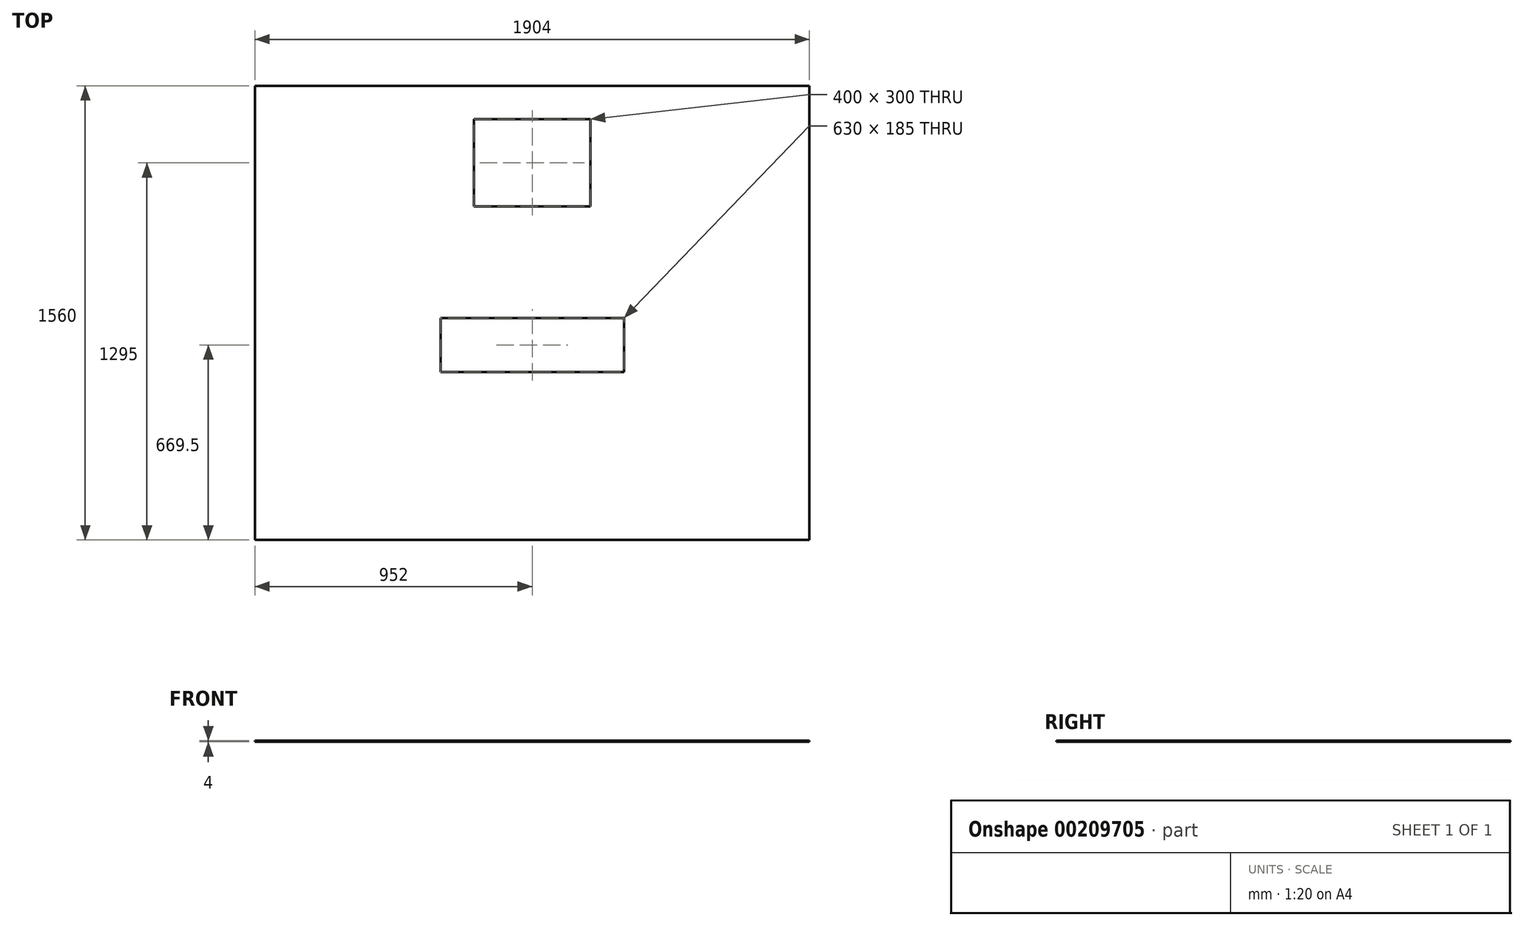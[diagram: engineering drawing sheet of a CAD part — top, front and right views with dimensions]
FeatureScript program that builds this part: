
annotation { "Feature Type Name" : "Feature", "Feature Type Description" : "" }
export const myFeature = defineFeature(function(context is Context, id is Id, definition is map)
    precondition{}
    {
        {
            var Q0;
            Q0=qCreatedBy(makeId("Top.planeOp"),FACE);
            var sketch = newSketch(context, id + "F0", { "sketchPlane" : qUnion([Q0])});
            skLineSegment(sketch, "E0.bottom", {"start": v(952, -780) * mm, "end": v(-952, -780) * mm});
            skLineSegment(sketch, "E0.top", {"start": v(952, 780) * mm, "end": v(-952, 780) * mm});
            skLineSegment(sketch, "E0.left", {"start": v(952, -780) * mm, "end": v(952, 780) * mm});
            skLineSegment(sketch, "E0.right", {"start": v(-952, -780) * mm, "end": v(-952, 780) * mm});
            skPoint(sketch, "E0.middle", {"position": v(0, 0) * mm});
            skSolve(sketch);
        }
        {
            var Q0;
            Q0=qSketchRegion(id+"F0",true);
            extrude(context, id + "F1", {"entities" : qUnion([Q0]), "depth" : 4 * mm});
        }
        {
            var Q0;
            Q0=makeQuery(id+"F1.opExtrude","CAP_FACE",FACE,{"disambiguationData":[OSD([sQuery(id+"F0.wireOp",EDGE,"E0.bottom"),sQuery(id+"F0.wireOp",EDGE,"E0.top"),sQuery(id+"F0.wireOp",EDGE,"E0.left"),sQuery(id+"F0.wireOp",EDGE,"E0.right")])],"isStart":false});
            var sketch = newSketch(context, id + "F2", { "sketchPlane" : qUnion([Q0])});
            skLineSegment(sketch, "E1", {"start": v(0, 780) * mm, "end": v(0, -780) * mm, "construction": true});
            skLineSegment(sketch, "E2.bottom", {"start": v(315, -203) * mm, "end": v(-315, -203) * mm});
            skLineSegment(sketch, "E2.top", {"start": v(315, -18) * mm, "end": v(-315, -18) * mm});
            skLineSegment(sketch, "E2.left", {"start": v(315, -203) * mm, "end": v(315, -18) * mm});
            skLineSegment(sketch, "E2.right", {"start": v(-315, -203) * mm, "end": v(-315, -18) * mm});
            skPoint(sketch, "E2.middle", {"position": v(0, -110.5) * mm});
            skLineSegment(sketch, "E3.bottom", {"start": v(200, 365) * mm, "end": v(-200, 365) * mm});
            skLineSegment(sketch, "E3.top", {"start": v(200, 665) * mm, "end": v(-200, 665) * mm});
            skLineSegment(sketch, "E3.left", {"start": v(200, 365) * mm, "end": v(200, 665) * mm});
            skLineSegment(sketch, "E3.right", {"start": v(-200, 365) * mm, "end": v(-200, 665) * mm});
            skPoint(sketch, "E3.middle", {"position": v(0, 515) * mm});
            skSolve(sketch);
        }
        {
            var Q0;
            Q0=qSketchRegion(id+"F2",true);
            extrude(context, id + "F3", {"entities" : qUnion([Q0]), "operationType" : NewBodyOperationType.REMOVE, "endBound" : BoundingType.THROUGH_ALL, "oppositeDirection" : true, "depth" : 25 * mm});
        }
    });
